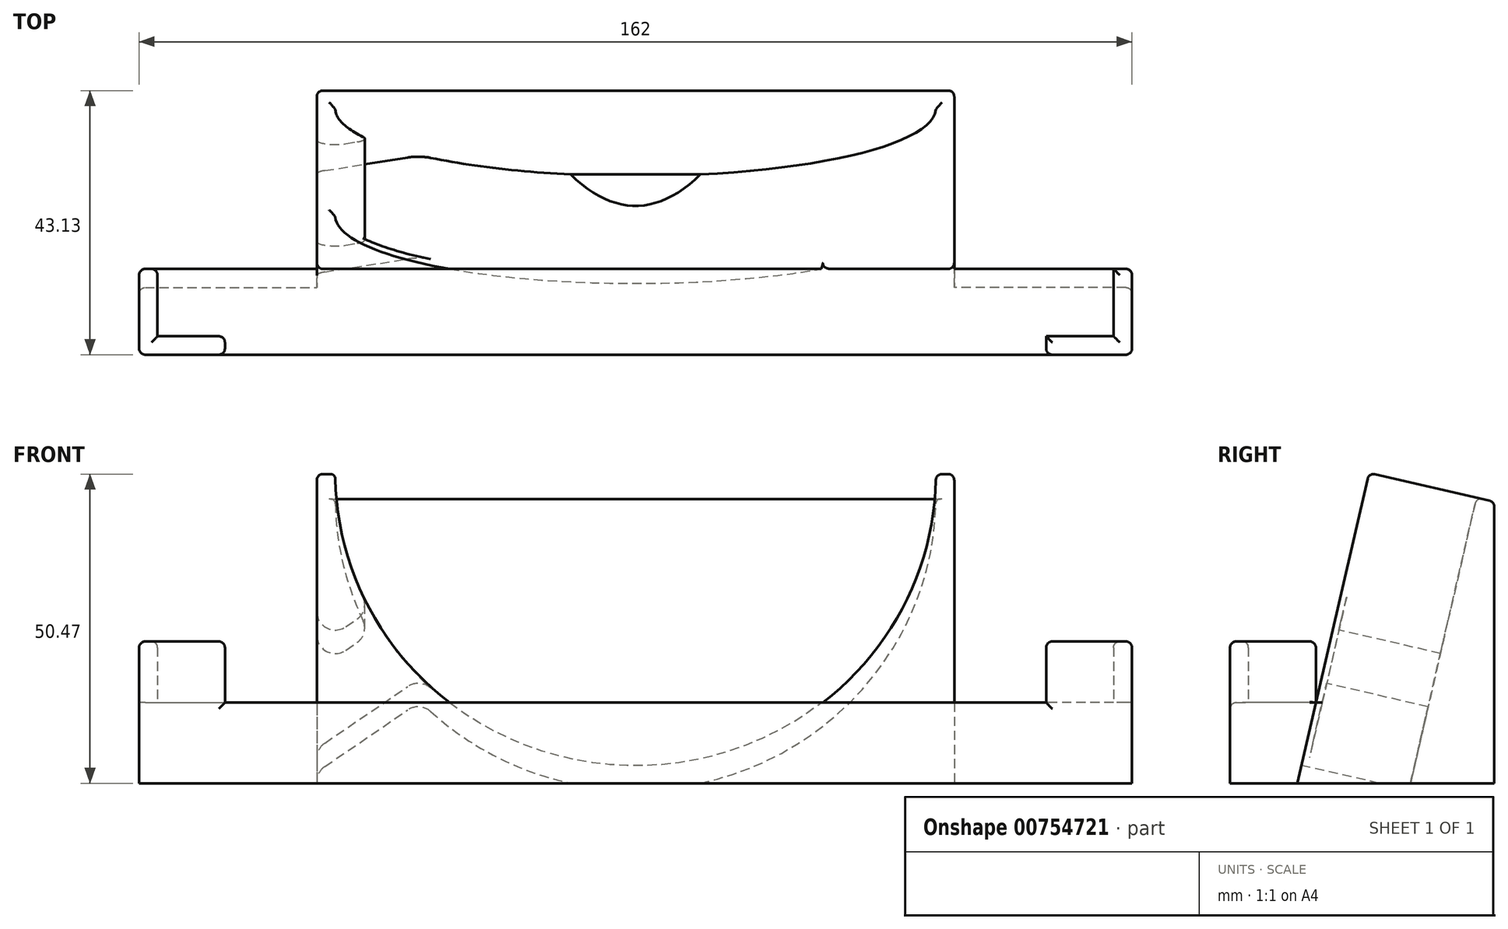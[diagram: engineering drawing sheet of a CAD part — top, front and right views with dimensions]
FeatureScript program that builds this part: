
annotation { "Feature Type Name" : "Feature", "Feature Type Description" : "" }
export const myFeature = defineFeature(function(context is Context, id is Id, definition is map)
    precondition{}
    {
        {
            var Q0;
            Q0=qCreatedBy(makeId("Right.planeOp"),FACE);
            var sketch = newSketch(context, id + "F0", { "sketchPlane" : qUnion([Q0])});
            skLineSegment(sketch, "E0", {"start": v(-55.45, -33.4) * mm, "end": v(107.34, -33.4) * mm});
            skLineSegment(sketch, "E1", {"start": v(-32.06, 67.93) * mm, "end": v(-11.6, 63.2) * mm});
            skLineSegment(sketch, "E2", {"start": v(-11.6, 63.2) * mm, "end": v(-11.6, -33.4) * mm});
            skLineSegment(sketch, "E3", {"start": v(-11.6, 63.2) * mm, "end": v(-33.9, -33.4) * mm});
            skLineSegment(sketch, "E4", {"start": v(-52.42, -20.25) * mm, "end": v(-66.42, -20.25) * mm});
            skLineSegment(sketch, "E5", {"start": v(-66.42, -20.25) * mm, "end": v(-66.42, -33.4) * mm});
            skLineSegment(sketch, "E6", {"start": v(-66.42, -33.4) * mm, "end": v(-47.42, -33.4) * mm});
            skLineSegment(sketch, "E7", {"start": v(-32.06, 67.93) * mm, "end": v(-55.45, -33.4) * mm});
            skLineSegment(sketch, "E8", {"start": v(-43.76, 17.26) * mm, "end": v(-23.3, 12.54) * mm});
            skLineSegment(sketch, "E9", {"start": v(-23.3, 12.54) * mm, "end": v(-23.3, -33.4) * mm});
            skSolve(sketch);
        }
        {
            var Q0;
            {var subQ3=sQuery(id+"F0.wireOp",EDGE,"E9");Q0=makeQuery(id+"F0.imprint","IMPRINT",FACE,{"disambiguationData":[TD([[makeQuery(id+"F0.imprint","IMPRINT",EDGE,{"derivedFrom":subQ3}),-1.0]])]});}
            var Q1;
            {var subQ2=sQuery(id+"F0.wireOp",EDGE,"E8");Q1=makeQuery(id+"F0.imprint","IMPRINT",FACE,{"disambiguationData":[TD([[makeQuery(id+"F0.imprint","IMPRINT",EDGE,{"derivedFrom":subQ2}),-1.0]])]});}
            extrude(context, id + "F1", {"entities" : qUnion([Q0, Q1]), "oppositeDirection" : true, "depth" : 52 * mm, "offsetDistance" : 25 * mm});
        }
        {
            var Q0;
            {var subQ3=sQuery(id+"F0.wireOp",EDGE,"E9");Q0=makeQuery(id+"F0.imprint","IMPRINT",FACE,{"disambiguationData":[TD([[makeQuery(id+"F0.imprint","IMPRINT",EDGE,{"derivedFrom":subQ3}),-1.0]])]});}
            var Q1;
            {var subQ2=sQuery(id+"F0.wireOp",EDGE,"E8");Q1=makeQuery(id+"F0.imprint","IMPRINT",FACE,{"disambiguationData":[TD([[makeQuery(id+"F0.imprint","IMPRINT",EDGE,{"derivedFrom":subQ2}),-1.0]])]});}
            extrude(context, id + "F2", {"entities" : qUnion([Q0, Q1]), "operationType" : NewBodyOperationType.ADD, "depth" : 52 * mm, "offsetDistance" : 25 * mm});
        }
        {
            var Q0;
            {var subQ0=sQuery(id+"F0.wireOp",EDGE,"E4");Q0=makeQuery(id+"F0.imprint","IMPRINT",FACE,{"disambiguationData":[TD([[makeQuery(id+"F0.imprint","IMPRINT",EDGE,{"derivedFrom":subQ0}),1.0]])]});}
            extrude(context, id + "F3", {"entities" : qUnion([Q0]), "operationType" : NewBodyOperationType.ADD, "depth" : 81 * mm, "offsetDistance" : 25 * mm});
        }
        {
            var Q0;
            {var subQ0=sQuery(id+"F0.wireOp",EDGE,"E4");Q0=makeQuery(id+"F0.imprint","IMPRINT",FACE,{"disambiguationData":[TD([[makeQuery(id+"F0.imprint","IMPRINT",EDGE,{"derivedFrom":subQ0}),1.0]])]});}
            extrude(context, id + "F4", {"entities" : qUnion([Q0]), "operationType" : NewBodyOperationType.ADD, "oppositeDirection" : true, "depth" : 81 * mm, "offsetDistance" : 25 * mm});
        }
        {
            var Q0;
            {var subQ0=sQuery(id+"F0.wireOp",EDGE,"E7");Q0=makeQuery(id+"F2.boolean.opBoolean","MERGE",FACE,{"derivedFrom":[makeQuery(id+"F1.opExtrude","SWEPT_FACE",FACE,{"disambiguationData":[OSD([subQ0])]}),makeQuery(id+"F2.opExtrude","SWEPT_FACE",FACE,{"disambiguationData":[OSD([subQ0])]})]});}
            var sketch = newSketch(context, id + "F5", { "sketchPlane" : qUnion([Q0])});
            skCircle(sketch, "E10", {"center": v(0, 6.98) * mm, "radius": 49 * mm});
            skSolve(sketch);
        }
        {
            var Q0;
            Q0 = qSketchRegion(id + "F5", true);
            var Q1;
            {var subQ0=sQuery(id+"F5.wireOp",EDGE,"E10");var subQ1=sQuery(id+"F0.wireOp",EDGE,"E8");var subQ2=sQuery(id+"F0.wireOp",EDGE,"E7");var subQ3=makeQuery(id+"F2.boolean.opBoolean","MERGE",EDGE,{"derivedFrom":[makeQuery(id+"F1.opExtrude","SWEPT_EDGE",EDGE,{"disambiguationData":[OSD([subQ2,subQ1])]}),makeQuery(id+"F2.opExtrude","SWEPT_EDGE",EDGE,{"disambiguationData":[OSD([subQ2,subQ1])]})]});var subQ4=makeQuery(id+"F5.imprint","INTERSECT",VERTEX,{"disambiguationData":[OD(0.0)],"derivedFrom":[subQ3,subQ0]});Q1=makeQuery(id+"F5.imprint","IMPRINT",FACE,{"disambiguationData":[TD([[makeQuery(id+"F5.imprint","IMPRINT",EDGE,{"disambiguationData":[TD([[subQ4,-1.0]])],"derivedFrom":subQ0}),1.0]])]});}
            extrude(context, id + "F6", {"entities" : qUnion([Q0, Q1]), "operationType" : NewBodyOperationType.REMOVE, "oppositeDirection" : true, "depth" : 18 * mm, "offsetDistance" : 25 * mm});
        }
        {
            var Q0;
            {var subQ0=sQuery(id+"F0.wireOp",EDGE,"E4");Q0=makeQuery(id+"F4.boolean.opBoolean","MERGE",FACE,{"derivedFrom":[makeQuery(id+"F3.opExtrude","SWEPT_FACE",FACE,{"disambiguationData":[OSD([subQ0])]}),makeQuery(id+"F4.opExtrude","SWEPT_FACE",FACE,{"disambiguationData":[OSD([subQ0])]})]});}
            var sketch = newSketch(context, id + "F7", { "sketchPlane" : qUnion([Q0])});
            skLineSegment(sketch, "E11.bottom", {"start": v(-81, -52.42) * mm, "end": v(-78, -52.42) * mm});
            skLineSegment(sketch, "E11.top", {"start": v(-81, -66.42) * mm, "end": v(-78, -66.42) * mm});
            skLineSegment(sketch, "E11.left", {"start": v(-81, -52.42) * mm, "end": v(-81, -66.42) * mm});
            skLineSegment(sketch, "E11.right", {"start": v(-78, -52.42) * mm, "end": v(-78, -63.42) * mm});
            skLineSegment(sketch, "E12.bottom", {"start": v(-81, -66.42) * mm, "end": v(-67, -66.42) * mm});
            skLineSegment(sketch, "E12.top", {"start": v(-78, -63.42) * mm, "end": v(-67, -63.42) * mm});
            skLineSegment(sketch, "E12.left", {"start": v(-81, -66.42) * mm, "end": v(-81, -63.42) * mm});
            skLineSegment(sketch, "E12.right", {"start": v(-67, -66.42) * mm, "end": v(-67, -63.42) * mm});
            skLineSegment(sketch, "E13.bottom", {"start": v(81, -52.42) * mm, "end": v(78, -52.42) * mm});
            skLineSegment(sketch, "E13.top", {"start": v(81, -66.42) * mm, "end": v(78, -66.42) * mm});
            skLineSegment(sketch, "E13.left", {"start": v(81, -52.42) * mm, "end": v(81, -66.42) * mm});
            skLineSegment(sketch, "E13.right", {"start": v(78, -52.42) * mm, "end": v(78, -63.42) * mm});
            skLineSegment(sketch, "E14.bottom", {"start": v(81, -66.42) * mm, "end": v(67, -66.42) * mm});
            skLineSegment(sketch, "E14.top", {"start": v(78, -63.42) * mm, "end": v(67, -63.42) * mm});
            skLineSegment(sketch, "E14.left", {"start": v(81, -66.42) * mm, "end": v(81, -63.42) * mm});
            skLineSegment(sketch, "E14.right", {"start": v(67, -66.42) * mm, "end": v(67, -63.42) * mm});
            skSolve(sketch);
        }
        {
            var Q0;
            Q0=makeQuery(id+"F7.imprint","IMPRINT",FACE,{"disambiguationData":[TD([[makeQuery(id+"F7.imprint","IMPRINT",EDGE,{"derivedFrom":sQuery(id+"F7.wireOp",EDGE,"E11.bottom")}),-1.0]])]});
            var Q1;
            Q1=makeQuery(id+"F7.imprint","IMPRINT",FACE,{"disambiguationData":[TD([[makeQuery(id+"F7.imprint","IMPRINT",EDGE,{"derivedFrom":sQuery(id+"F7.wireOp",EDGE,"E13.bottom")}),1.0]])]});
            extrude(context, id + "F8", {"entities" : qUnion([Q0, Q1]), "operationType" : NewBodyOperationType.ADD, "depth" : 10 * mm, "offsetDistance" : 25 * mm});
        }
        {
            var Q0;
            {var subQ0=sQuery(id+"F0.wireOp",EDGE,"E9");var subQ1=sQuery(id+"F0.wireOp",EDGE,"E8");var subQ2=sQuery(id+"F0.wireOp",EDGE,"E3");Q0=makeQuery(id+"F2.boolean.opBoolean","MERGE",EDGE,{"derivedFrom":[makeQuery(id+"F1.opExtrude","SWEPT_EDGE",EDGE,{"disambiguationData":[OSD([subQ2,subQ1,subQ0])]}),makeQuery(id+"F2.opExtrude","SWEPT_EDGE",EDGE,{"disambiguationData":[OSD([subQ2,subQ1,subQ0])]})]});}
            var Q1;
            {var subQ0=sQuery(id+"F0.wireOp",EDGE,"E8");Q1=makeQuery(id+"F6.boolean.opBoolean","INTERSECT",EDGE,{"derivedFrom":[makeQuery(id+"F2.boolean.opBoolean","MERGE",FACE,{"derivedFrom":[makeQuery(id+"F1.opExtrude","SWEPT_FACE",FACE,{"disambiguationData":[OSD([subQ0])]}),makeQuery(id+"F2.opExtrude","SWEPT_FACE",FACE,{"disambiguationData":[OSD([subQ0])]})]}),makeQuery(id+"F6.opExtrude","CAP_FACE",FACE,{"disambiguationData":[OSD([sQuery(id+"F5.wireOp",EDGE,"E10")])],"isStart":false})]});}
            var Q2;
            Q2=makeQuery(id+"F1.opExtrude","CAP_EDGE",EDGE,{"disambiguationData":[OSD([sQuery(id+"F0.wireOp",EDGE,"E8")])],"isStart":false});
            var Q3;
            {var subQ0=sQuery(id+"F0.wireOp",EDGE,"E8");Q3=makeQuery(id+"F6.boolean.opBoolean","INTERSECT",EDGE,{"disambiguationData":[OD(0.0)],"derivedFrom":[makeQuery(id+"F2.boolean.opBoolean","MERGE",FACE,{"derivedFrom":[makeQuery(id+"F1.opExtrude","SWEPT_FACE",FACE,{"disambiguationData":[OSD([subQ0])]}),makeQuery(id+"F2.opExtrude","SWEPT_FACE",FACE,{"disambiguationData":[OSD([subQ0])]})]}),makeQuery(id+"F6.opExtrude","SWEPT_FACE",FACE,{"disambiguationData":[OSD([sQuery(id+"F5.wireOp",EDGE,"E10")])]})]});}
            var Q4;
            {var subQ0=sQuery(id+"F0.wireOp",EDGE,"E7");var subQ1=sQuery(id+"F5.wireOp",EDGE,"E10");Q4=makeQuery(id+"F6.boolean.opBoolean","COPY",EDGE,{"disambiguationData":[topologyDisambiguationEdgeConnected([makeQuery(id+"F1.opExtrude","SWEPT_FACE",FACE,{"disambiguationData":[OSD([subQ0])]}),makeQuery(id+"F2.opExtrude","SWEPT_FACE",FACE,{"disambiguationData":[OSD([subQ0])]}),makeQuery(id+"F6.opExtrude","SWEPT_FACE",FACE,{"disambiguationData":[OSD([subQ1])]})]),OD(1.0)],"derivedFrom":makeQuery(id+"F6.opExtrude","CAP_EDGE",EDGE,{"disambiguationData":[OSD([subQ1])],"isStart":true})});}
            var Q5;
            {var subQ0=sQuery(id+"F0.wireOp",EDGE,"E8");Q5=makeQuery(id+"F6.boolean.opBoolean","INTERSECT",EDGE,{"disambiguationData":[OD(1.0)],"derivedFrom":[makeQuery(id+"F2.boolean.opBoolean","MERGE",FACE,{"derivedFrom":[makeQuery(id+"F1.opExtrude","SWEPT_FACE",FACE,{"disambiguationData":[OSD([subQ0])]}),makeQuery(id+"F2.opExtrude","SWEPT_FACE",FACE,{"disambiguationData":[OSD([subQ0])]})]}),makeQuery(id+"F6.opExtrude","SWEPT_FACE",FACE,{"disambiguationData":[OSD([sQuery(id+"F5.wireOp",EDGE,"E10")])]})]});}
            var Q6;
            Q6=makeQuery(id+"F2.opExtrude","CAP_EDGE",EDGE,{"disambiguationData":[OSD([sQuery(id+"F0.wireOp",EDGE,"E9")])],"isStart":false});
            var Q7;
            {var subQ0=sQuery(id+"F0.wireOp",EDGE,"E7");var subQ1=sQuery(id+"F5.wireOp",EDGE,"E10");Q7=makeQuery(id+"F6.boolean.opBoolean","COPY",EDGE,{"disambiguationData":[topologyDisambiguationEdgeConnected([makeQuery(id+"F1.opExtrude","SWEPT_FACE",FACE,{"disambiguationData":[OSD([subQ0])]}),makeQuery(id+"F2.opExtrude","SWEPT_FACE",FACE,{"disambiguationData":[OSD([subQ0])]}),makeQuery(id+"F6.opExtrude","SWEPT_FACE",FACE,{"disambiguationData":[OSD([subQ1])]})]),OD(0.0)],"derivedFrom":makeQuery(id+"F6.opExtrude","CAP_EDGE",EDGE,{"disambiguationData":[OSD([subQ1])],"isStart":true})});}
            var Q8;
            Q8=makeQuery(id+"F8.opExtrude","CAP_EDGE",EDGE,{"disambiguationData":[OSD([sQuery(id+"F7.wireOp",EDGE,"E13.bottom")])],"isStart":false});
            var Q9;
            Q9=makeQuery(id+"F8.opExtrude","CAP_EDGE",EDGE,{"disambiguationData":[OSD([sQuery(id+"F7.wireOp",EDGE,"E14.top")])],"isStart":false});
            var Q10;
            Q10=makeQuery(id+"F8.opExtrude","CAP_EDGE",EDGE,{"disambiguationData":[OSD([sQuery(id+"F7.wireOp",EDGE,"E13.right")])],"isStart":false});
            var Q11;
            Q11=makeQuery(id+"F8.opExtrude","CAP_EDGE",EDGE,{"disambiguationData":[OSD([sQuery(id+"F7.wireOp",EDGE,"E14.right")])],"isStart":false});
            var Q12;
            Q12=makeQuery(id+"F8.opExtrude","CAP_EDGE",EDGE,{"disambiguationData":[OSD([sQuery(id+"F7.wireOp",EDGE,"E14.bottom")])],"isStart":false});
            var Q13;
            Q13=makeQuery(id+"F8.opExtrude","CAP_EDGE",EDGE,{"disambiguationData":[OSD([sQuery(id+"F7.wireOp",EDGE,"E13.left"),sQuery(id+"F7.wireOp",EDGE,"E14.left")])],"isStart":false});
            var Q14;
            {var subQ0=sQuery(id+"F0.wireOp",EDGE,"E5");var subQ1=sQuery(id+"F0.wireOp",EDGE,"E4");Q14=makeQuery(id+"F4.boolean.opBoolean","MERGE",EDGE,{"derivedFrom":[makeQuery(id+"F3.opExtrude","SWEPT_EDGE",EDGE,{"disambiguationData":[OSD([subQ1,subQ0])]}),makeQuery(id+"F4.opExtrude","SWEPT_EDGE",EDGE,{"disambiguationData":[OSD([subQ1,subQ0])]})]});}
            var Q15;
            Q15=makeQuery(id+"F8.opExtrude","SWEPT_EDGE",EDGE,{"disambiguationData":[OSD([sQuery(id+"F0.wireOp",EDGE,"E4"),sQuery(id+"F0.wireOp",EDGE,"E5"),sQuery(id+"F7.wireOp",EDGE,"E14.bottom"),sQuery(id+"F7.wireOp",EDGE,"E14.right")])]});
            var Q16;
            Q16=makeQuery(id+"F8.boolean.opBoolean","MERGE",EDGE,{"derivedFrom":[makeQuery(id+"F3.opExtrude","CAP_EDGE",EDGE,{"disambiguationData":[OSD([sQuery(id+"F0.wireOp",EDGE,"E5")])],"isStart":false}),makeQuery(id+"F8.opExtrude","SWEPT_EDGE",EDGE,{"disambiguationData":[OSD([sQuery(id+"F7.wireOp",EDGE,"E14.bottom"),sQuery(id+"F7.wireOp",EDGE,"E14.left")])]})]});
            var Q17;
            Q17=makeQuery(id+"F8.opExtrude","SWEPT_EDGE",EDGE,{"disambiguationData":[OSD([sQuery(id+"F0.wireOp",EDGE,"E4"),sQuery(id+"F0.wireOp",EDGE,"E5"),sQuery(id+"F7.wireOp",EDGE,"E12.bottom"),sQuery(id+"F7.wireOp",EDGE,"E12.right")])]});
            var Q18;
            Q18=makeQuery(id+"F8.opExtrude","CAP_EDGE",EDGE,{"disambiguationData":[OSD([sQuery(id+"F7.wireOp",EDGE,"E12.right")])],"isStart":false});
            var Q19;
            Q19=makeQuery(id+"F8.opExtrude","CAP_EDGE",EDGE,{"disambiguationData":[OSD([sQuery(id+"F7.wireOp",EDGE,"E12.top")])],"isStart":false});
            var Q20;
            Q20=makeQuery(id+"F8.opExtrude","CAP_EDGE",EDGE,{"disambiguationData":[OSD([sQuery(id+"F7.wireOp",EDGE,"E12.bottom")])],"isStart":false});
            var Q21;
            Q21=makeQuery(id+"F8.opExtrude","CAP_EDGE",EDGE,{"disambiguationData":[OSD([sQuery(id+"F7.wireOp",EDGE,"E11.left"),sQuery(id+"F7.wireOp",EDGE,"E12.left")])],"isStart":false});
            var Q22;
            Q22=makeQuery(id+"F8.opExtrude","CAP_EDGE",EDGE,{"disambiguationData":[OSD([sQuery(id+"F7.wireOp",EDGE,"E11.right")])],"isStart":false});
            var Q23;
            Q23=makeQuery(id+"F8.opExtrude","CAP_EDGE",EDGE,{"disambiguationData":[OSD([sQuery(id+"F7.wireOp",EDGE,"E11.bottom")])],"isStart":false});
            var Q24;
            Q24=makeQuery(id+"F8.boolean.opBoolean","MERGE",EDGE,{"derivedFrom":[makeQuery(id+"F4.opExtrude","CAP_EDGE",EDGE,{"disambiguationData":[OSD([sQuery(id+"F0.wireOp",EDGE,"E5")])],"isStart":false}),makeQuery(id+"F8.opExtrude","SWEPT_EDGE",EDGE,{"disambiguationData":[OSD([sQuery(id+"F7.wireOp",EDGE,"E12.bottom"),sQuery(id+"F7.wireOp",EDGE,"E12.left")])]})]});
            var Q25;
            {var subQ0=sQuery(id+"F0.wireOp",EDGE,"E7");Q25=makeQuery(id+"F3.boolean.opBoolean","SPLIT",EDGE,{"disambiguationData":[topologyDisambiguationEdgeConnected([makeQuery(id+"F1.opExtrude","SWEPT_FACE",FACE,{"disambiguationData":[OSD([subQ0])]})])],"derivedFrom":makeQuery(id+"F2.opExtrude","CAP_EDGE",EDGE,{"disambiguationData":[OSD([subQ0])],"isStart":false})});}
            var Q26;
            {var subQ0=sQuery(id+"F0.wireOp",EDGE,"E7");var subQ1=sQuery(id+"F0.wireOp",EDGE,"E8");Q26=makeQuery(id+"F6.boolean.opBoolean","SPLIT",EDGE,{"disambiguationData":[TD([makeQuery(id+"F2.opExtrude","CAP_FACE",FACE,{"disambiguationData":[OSD([sQuery(id+"F0.wireOp",EDGE,"E0"),sQuery(id+"F0.wireOp",EDGE,"E6"),subQ0,subQ1,sQuery(id+"F0.wireOp",EDGE,"E9")])],"isStart":false})])],"derivedFrom":makeQuery(id+"F2.boolean.opBoolean","MERGE",EDGE,{"derivedFrom":[makeQuery(id+"F1.opExtrude","SWEPT_EDGE",EDGE,{"disambiguationData":[OSD([subQ0,subQ1])]}),makeQuery(id+"F2.opExtrude","SWEPT_EDGE",EDGE,{"disambiguationData":[OSD([subQ0,subQ1])]})]})});}
            var Q27;
            Q27=makeQuery(id+"F2.opExtrude","CAP_EDGE",EDGE,{"disambiguationData":[OSD([sQuery(id+"F0.wireOp",EDGE,"E8")])],"isStart":false});
            var Q28;
            {var subQ0=sQuery(id+"F0.wireOp",EDGE,"E7");Q28=makeQuery(id+"F4.boolean.opBoolean","SPLIT",EDGE,{"disambiguationData":[topologyDisambiguationEdgeConnected([makeQuery(id+"F1.opExtrude","SWEPT_FACE",FACE,{"disambiguationData":[OSD([subQ0])]})])],"derivedFrom":makeQuery(id+"F1.opExtrude","CAP_EDGE",EDGE,{"disambiguationData":[OSD([subQ0])],"isStart":false})});}
            var Q29;
            {var subQ0=sQuery(id+"F0.wireOp",EDGE,"E7");var subQ1=sQuery(id+"F0.wireOp",EDGE,"E8");Q29=makeQuery(id+"F6.boolean.opBoolean","SPLIT",EDGE,{"disambiguationData":[TD([makeQuery(id+"F1.opExtrude","CAP_FACE",FACE,{"disambiguationData":[OSD([sQuery(id+"F0.wireOp",EDGE,"E0"),sQuery(id+"F0.wireOp",EDGE,"E6"),subQ0,subQ1,sQuery(id+"F0.wireOp",EDGE,"E9")])],"isStart":false})])],"derivedFrom":makeQuery(id+"F2.boolean.opBoolean","MERGE",EDGE,{"derivedFrom":[makeQuery(id+"F1.opExtrude","SWEPT_EDGE",EDGE,{"disambiguationData":[OSD([subQ0,subQ1])]}),makeQuery(id+"F2.opExtrude","SWEPT_EDGE",EDGE,{"disambiguationData":[OSD([subQ0,subQ1])]})]})});}
            var Q30;
            Q30=makeQuery(id+"F1.opExtrude","CAP_EDGE",EDGE,{"disambiguationData":[OSD([sQuery(id+"F0.wireOp",EDGE,"E9")])],"isStart":false});
            var Q31;
            Q31=makeQuery(id+"F8.opExtrude","SWEPT_EDGE",EDGE,{"disambiguationData":[OSD([sQuery(id+"F7.wireOp",EDGE,"E12.top"),sQuery(id+"F7.wireOp",EDGE,"E12.right")])]});
            var Q32;
            Q32=makeQuery(id+"F8.opExtrude","SWEPT_EDGE",EDGE,{"disambiguationData":[OSD([sQuery(id+"F0.wireOp",EDGE,"E4"),sQuery(id+"F0.wireOp",EDGE,"E7"),sQuery(id+"F7.wireOp",EDGE,"E11.bottom"),sQuery(id+"F7.wireOp",EDGE,"E11.right")])]});
            var Q33;
            Q33=makeQuery(id+"F8.opExtrude","SWEPT_EDGE",EDGE,{"disambiguationData":[OSD([sQuery(id+"F7.wireOp",EDGE,"E11.bottom"),sQuery(id+"F7.wireOp",EDGE,"E11.left")])]});
            var Q34;
            Q34=makeQuery(id+"F4.opExtrude","CAP_EDGE",EDGE,{"disambiguationData":[OSD([sQuery(id+"F0.wireOp",EDGE,"E7")])],"isStart":false});
            var Q35;
            Q35=makeQuery(id+"F8.opExtrude","SWEPT_EDGE",EDGE,{"disambiguationData":[OSD([sQuery(id+"F7.wireOp",EDGE,"E13.bottom"),sQuery(id+"F7.wireOp",EDGE,"E13.left")])]});
            var Q36;
            Q36=makeQuery(id+"F3.opExtrude","CAP_EDGE",EDGE,{"disambiguationData":[OSD([sQuery(id+"F0.wireOp",EDGE,"E7")])],"isStart":false});
            fillet(context, id + "F9", {"entities" : qUnion([Q0, Q1, Q2, Q3, Q4, Q5, Q6, Q7, Q8, Q9, Q10, Q11, Q12, Q13, Q14, Q15, Q16, Q17, Q18, Q19, Q20, Q21, Q22, Q23, Q24, Q25, Q26, Q27, Q28, Q29, Q30, Q31, Q32, Q33, Q34, Q35, Q36]), "radius" : 1 * mm, "tangentPropagation" : true, "allowEdgeOverflow" : false});
        }
        {
            var Q0;
            Q0=makeQuery(id+"F6.boolean.opBoolean","COPY",FACE,{"derivedFrom":makeQuery(id+"F6.opExtrude","CAP_FACE",FACE,{"disambiguationData":[OSD([sQuery(id+"F5.wireOp",EDGE,"E10")])],"isStart":false})});
            var sketch = newSketch(context, id + "F10", { "sketchPlane" : qUnion([Q0])});
            skLineSegment(sketch, "E15", {"start": v(0, 5.98) * mm, "end": v(-39.66, -21.8) * mm});
            skLineSegment(sketch, "E16.0", {"start": v(-4.02, 11.7) * mm, "end": v(-43.62, -16.02) * mm});
            skLineSegment(sketch, "E17.0", {"start": v(4.02, 0.24) * mm, "end": v(-35.6, -27.5) * mm});
            skLineSegment(sketch, "E18", {"start": v(-42.06, -14.93) * mm, "end": v(-34.03, -26.4) * mm});
            skLineSegment(sketch, "E19", {"start": v(-29.88, -6.4) * mm, "end": v(-21.85, -17.87) * mm});
            skSolve(sketch);
        }
        {
            var Q0;
            {var subQ0=sQuery(id+"F10.wireOp",EDGE,"E19");var subQ1=sQuery(id+"F10.wireOp",EDGE,"E15");var subQ2=makeQuery(id+"F10.imprint","INTERSECT",VERTEX,{"derivedFrom":[subQ1,subQ0]});Q0=makeQuery(id+"F10.imprint","IMPRINT",FACE,{"disambiguationData":[TD([[makeQuery(id+"F10.imprint","IMPRINT",EDGE,{"disambiguationData":[TD([[subQ2,-1.0]])],"derivedFrom":subQ1}),-1.0]])]});}
            var Q1;
            {var subQ0=sQuery(id+"F10.wireOp",EDGE,"E19");var subQ1=sQuery(id+"F10.wireOp",EDGE,"E15");var subQ2=makeQuery(id+"F10.imprint","INTERSECT",VERTEX,{"derivedFrom":[subQ1,subQ0]});Q1=makeQuery(id+"F10.imprint","IMPRINT",FACE,{"disambiguationData":[TD([[makeQuery(id+"F10.imprint","IMPRINT",EDGE,{"disambiguationData":[TD([[subQ2,-1.0]])],"derivedFrom":subQ1}),1.0]])]});}
            extrude(context, id + "F11", {"entities" : qUnion([Q0, Q1]), "operationType" : NewBodyOperationType.ADD, "depth" : 17 * mm, "offsetDistance" : 25 * mm});
        }
        {
            var Q0;
            Q0=makeQuery(id+"F11.opExtrude","SWEPT_FACE",FACE,{"disambiguationData":[OSD([sQuery(id+"F10.wireOp",EDGE,"E19")])]});
            extrude(context, id + "F12", {"entities" : qUnion([Q0]), "operationType" : NewBodyOperationType.REMOVE, "oppositeDirection" : true, "depth" : 40 * mm, "offsetDistance" : 25 * mm});
        }
        {
            var Q0;
            Q0=makeQuery(id+"F12.boolean.opBoolean","INTERSECT",EDGE,{"derivedFrom":[makeQuery(id+"F6.boolean.opBoolean","COPY",FACE,{"derivedFrom":makeQuery(id+"F6.opExtrude","SWEPT_FACE",FACE,{"disambiguationData":[OSD([sQuery(id+"F5.wireOp",EDGE,"E10")])]})}),makeQuery(id+"F12.opExtrude","SWEPT_FACE",FACE,{"disambiguationData":[OSD([sQuery(id+"F10.wireOp",EDGE,"E16.0"),sQuery(id+"F10.wireOp",EDGE,"E19")])]})]});
            var Q1;
            Q1=makeQuery(id+"F12.boolean.opBoolean","INTERSECT",EDGE,{"derivedFrom":[makeQuery(id+"F6.boolean.opBoolean","COPY",FACE,{"derivedFrom":makeQuery(id+"F6.opExtrude","SWEPT_FACE",FACE,{"disambiguationData":[OSD([sQuery(id+"F5.wireOp",EDGE,"E10")])]})}),makeQuery(id+"F12.opExtrude","SWEPT_FACE",FACE,{"disambiguationData":[OSD([sQuery(id+"F10.wireOp",EDGE,"E17.0"),sQuery(id+"F10.wireOp",EDGE,"E19")])]})]});
            var Q2;
            Q2=makeQuery(id+"F12.boolean.opBoolean","INTERSECT",EDGE,{"derivedFrom":[makeQuery(id+"F1.opExtrude","CAP_FACE",FACE,{"disambiguationData":[OSD([sQuery(id+"F0.wireOp",EDGE,"E0"),sQuery(id+"F0.wireOp",EDGE,"E6"),sQuery(id+"F0.wireOp",EDGE,"E7"),sQuery(id+"F0.wireOp",EDGE,"E8"),sQuery(id+"F0.wireOp",EDGE,"E9")])],"isStart":false}),makeQuery(id+"F12.opExtrude","SWEPT_FACE",FACE,{"disambiguationData":[OSD([sQuery(id+"F10.wireOp",EDGE,"E16.0"),sQuery(id+"F10.wireOp",EDGE,"E19")])]})]});
            var Q3;
            Q3=makeQuery(id+"F12.boolean.opBoolean","INTERSECT",EDGE,{"derivedFrom":[makeQuery(id+"F1.opExtrude","CAP_FACE",FACE,{"disambiguationData":[OSD([sQuery(id+"F0.wireOp",EDGE,"E0"),sQuery(id+"F0.wireOp",EDGE,"E6"),sQuery(id+"F0.wireOp",EDGE,"E7"),sQuery(id+"F0.wireOp",EDGE,"E8"),sQuery(id+"F0.wireOp",EDGE,"E9")])],"isStart":false}),makeQuery(id+"F12.opExtrude","SWEPT_FACE",FACE,{"disambiguationData":[OSD([sQuery(id+"F10.wireOp",EDGE,"E17.0"),sQuery(id+"F10.wireOp",EDGE,"E19")])]})]});
            fillet(context, id + "F13", {"entities" : qUnion([Q0, Q1, Q2, Q3]), "radius" : 3 * mm, "tangentPropagation" : true, "allowEdgeOverflow" : false});
        }
    });
